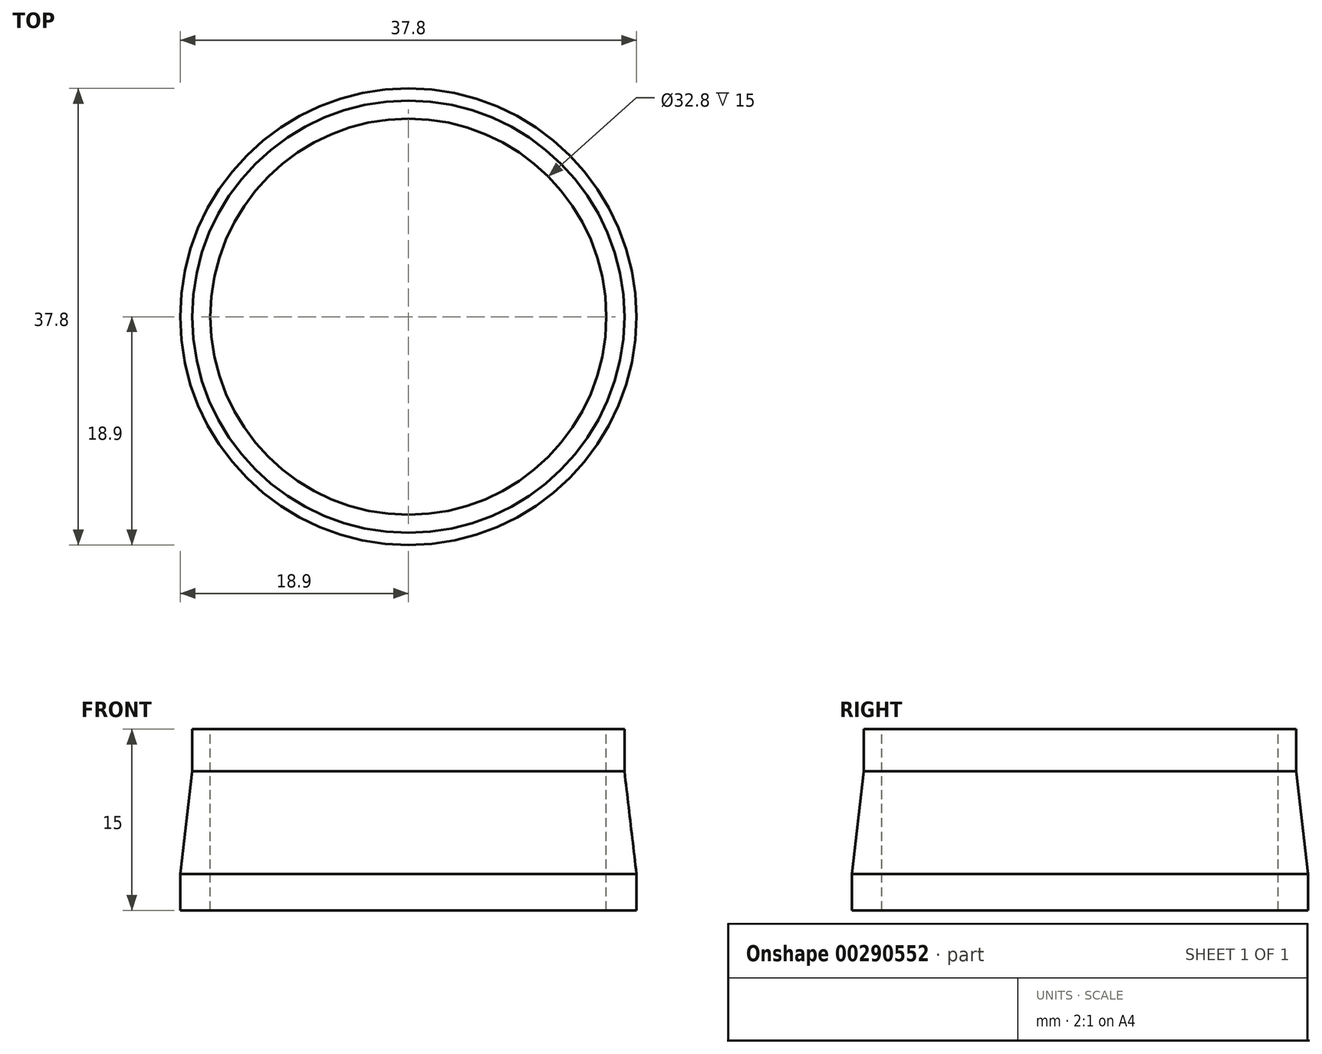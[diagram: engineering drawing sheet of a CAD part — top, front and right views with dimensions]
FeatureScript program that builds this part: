
annotation { "Feature Type Name" : "Feature", "Feature Type Description" : "" }
export const myFeature = defineFeature(function(context is Context, id is Id, definition is map)
    precondition{}
    {
        {
            var Q0;
            Q0=qCreatedBy(makeId("Front.planeOp"),FACE);
            var sketch = newSketch(context, id + "F0", { "sketchPlane" : qUnion([Q0])});
            skLineSegment(sketch, "E0", {"start": v(16.4, 0) * mm, "end": v(16.4, 15) * mm});
            skLineSegment(sketch, "E1", {"start": v(16.4, 15) * mm, "end": v(17.9, 15) * mm});
            skLineSegment(sketch, "E2", {"start": v(16.4, 0) * mm, "end": v(18.9, 0) * mm});
            skLineSegment(sketch, "E3", {"start": v(18.9, 0) * mm, "end": v(18.9, 3) * mm});
            skLineSegment(sketch, "E4", {"start": v(17.9, 15) * mm, "end": v(17.9, 11.5) * mm});
            skLineSegment(sketch, "E5", {"start": v(17.9, 11.5) * mm, "end": v(18.9, 3) * mm});
            skLineSegment(sketch, "E6", {"start": v(0, 0) * mm, "end": v(0, 69.89) * mm, "construction": true});
            skSolve(sketch);
        }
        {
            var Q0;
            Q0=sQuery(id+"F0.wireOp",EDGE,"E0");
            var Q1;
            Q1=sQuery(id+"F0.wireOp",EDGE,"E5");
            var Q2;
            Q2=sQuery(id+"F0.wireOp",EDGE,"E1");
            var Q3;
            Q3=sQuery(id+"F0.wireOp",EDGE,"E4");
            var Q4;
            Q4=sQuery(id+"F0.wireOp",EDGE,"E2");
            var Q5;
            Q5=sQuery(id+"F0.wireOp",EDGE,"E3");
            var Q6;
            Q6=sQuery(id+"F0.wireOp",EDGE,"E6");
            revolve(context, id + "F1", {"bodyType" : ToolBodyType.SURFACE, "surfaceEntities" : qUnion([Q0, Q1, Q2, Q3, Q4, Q5]), "axis" : qUnion([Q6]), "revolveType" : RevolveType.FULL});
        }
    });
